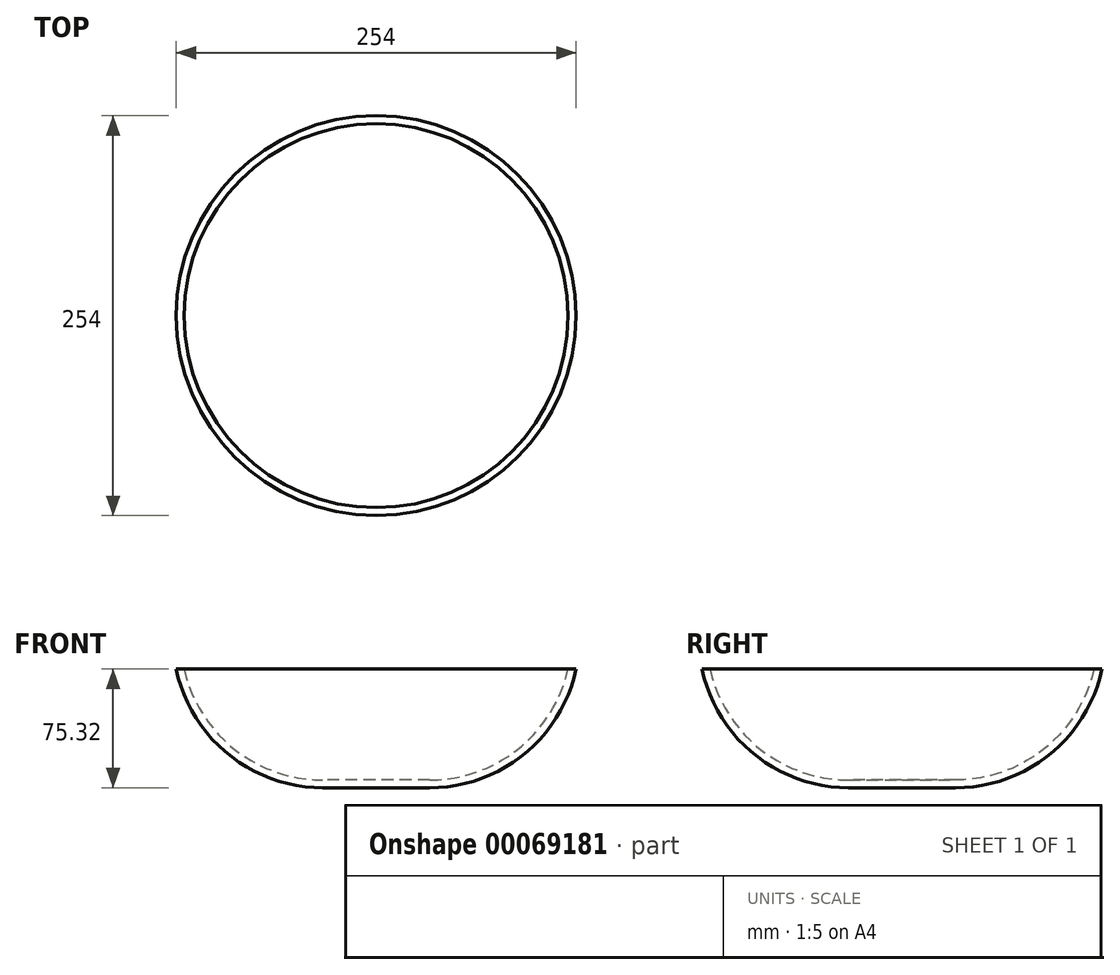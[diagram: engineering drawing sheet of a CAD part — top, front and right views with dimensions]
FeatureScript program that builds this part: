
annotation { "Feature Type Name" : "Feature", "Feature Type Description" : "" }
export const myFeature = defineFeature(function(context is Context, id is Id, definition is map)
    precondition{}
    {
        {
            var Q0;
            Q0=qCreatedBy(makeId("Front.planeOp"),FACE);
            var sketch = newSketch(context, id + "F0", { "sketchPlane" : qUnion([Q0])});
            skLineSegment(sketch, "E0", {"start": v(0, 7.66) * mm, "end": v(127, 7.66) * mm});
            skLineSegment(sketch, "E1", {"start": v(0, -67.66) * mm, "end": v(33.99, -67.66) * mm});
            skLineSegment(sketch, "E2", {"start": v(0, -61.33) * mm, "end": v(0, -67.66) * mm});
            skLineSegment(sketch, "E3", {"start": v(0, 7.66) * mm, "end": v(0, -61.33) * mm});
            skArc(sketch, "E4", {"start": v(33.99, -67.66) * mm, "mid": v(93.83, -46.47) * mm, "end": v(127, 7.66) * mm});
            skArc(sketch, "E5.0", {"start": v(33.99, -62.72) * mm, "mid": v(90.3, -42.96) * mm, "end": v(121.94, 7.66) * mm});
            skLineSegment(sketch, "E5.1", {"start": v(0, -62.72) * mm, "end": v(33.99, -62.72) * mm});
            skSolve(sketch);
        }
        {
            var Q0;
            {var subQ2=sQuery(id+"F0.wireOp",EDGE,"E1");Q0=makeQuery(id+"F0.imprint","IMPRINT",FACE,{"disambiguationData":[TD([[makeQuery(id+"F0.imprint","IMPRINT",EDGE,{"derivedFrom":subQ2}),1.0]])]});}
            var Q1;
            Q1=sQuery(id+"F0.wireOp",EDGE,"E3");
            revolve(context, id + "F1", {"entities" : qUnion([Q0]), "axis" : qUnion([Q1]), "revolveType" : RevolveType.FULL});
        }
    });
